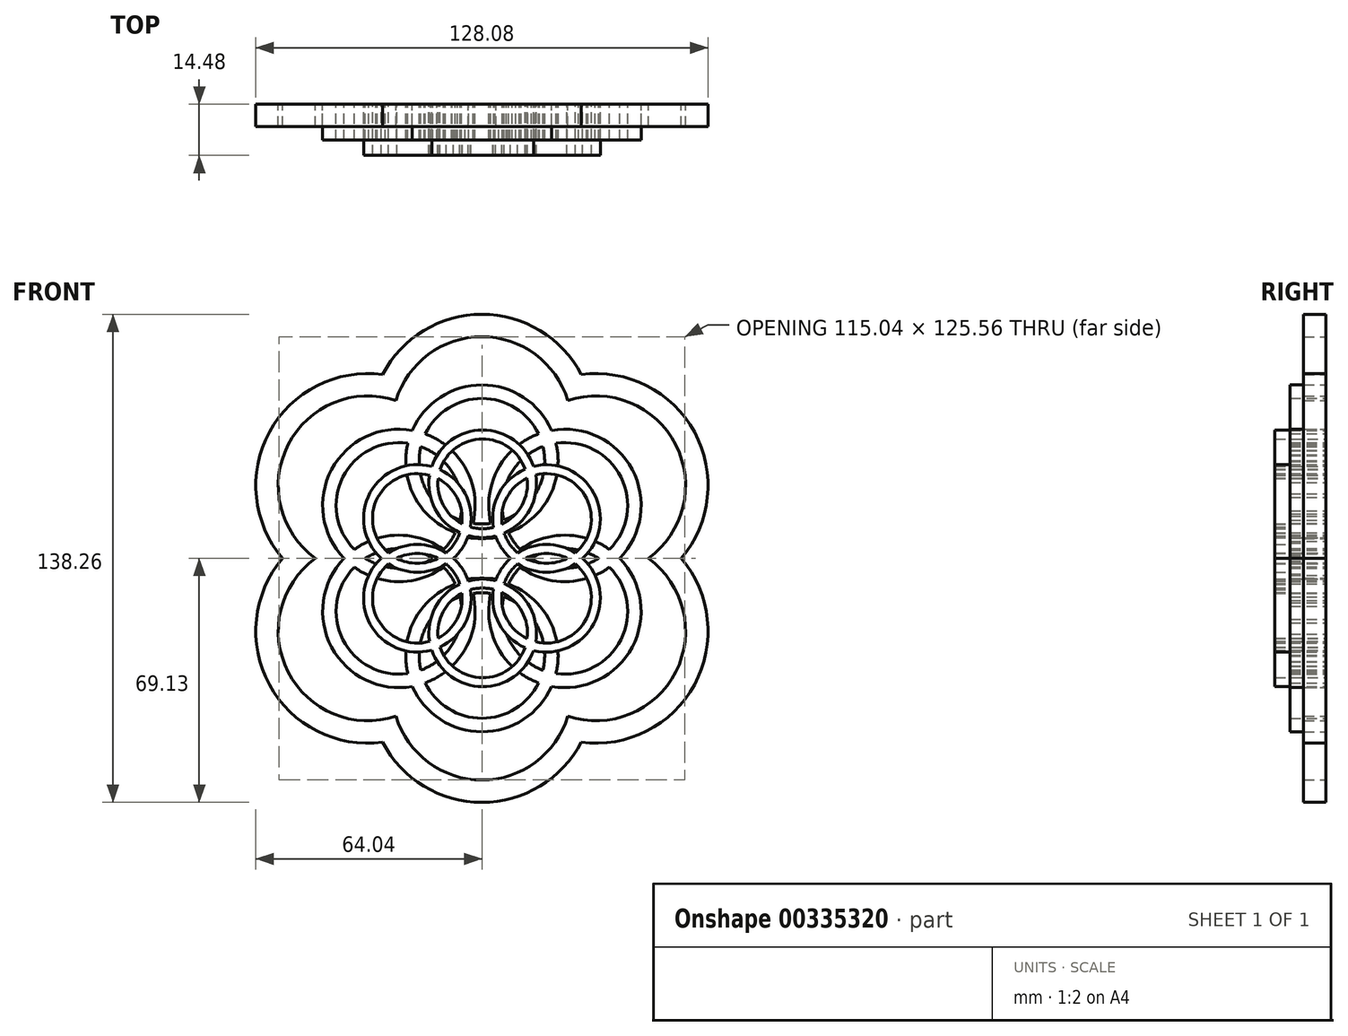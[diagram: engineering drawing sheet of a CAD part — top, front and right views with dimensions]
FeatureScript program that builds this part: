
annotation { "Feature Type Name" : "Feature", "Feature Type Description" : "" }
export const myFeature = defineFeature(function(context is Context, id is Id, definition is map)
    precondition{}
    {
        {
            var Q0;
            Q0=qCreatedBy(makeId("Front.planeOp"),FACE);
            var sketch = newSketch(context, id + "F0", { "sketchPlane" : qUnion([Q0])});
            skArc(sketch, "E0", {"start": v(-1.72, 12.04) * mm, "mid": v(-58.67, 38.27) * mm, "end": v(-12.73, -4.4) * mm});
            skArc(sketch, "E1", {"start": v(-7.98, 13.27) * mm, "mid": v(-52.97, 35.36) * mm, "end": v(-17.44, 0) * mm});
            skArc(sketch, "E2.MirrorC", {"start": v(8.14, 0) * mm, "mid": v(5.98, 2.84) * mm, "end": v(4.15, 5.9) * mm});
            skArc(sketch, "E3.MirrorC", {"start": v(12.73, 4.4) * mm, "mid": v(11.6, 5.88) * mm, "end": v(10.57, 7.44) * mm});
            skArc(sketch, "E4.MirrorC", {"start": v(7.98, -13.27) * mm, "mid": v(52.97, -35.36) * mm, "end": v(17.44, 0) * mm});
            skArc(sketch, "E5.MirrorC", {"start": v(1.72, -12.04) * mm, "mid": v(58.67, -38.27) * mm, "end": v(12.73, 4.4) * mm});
            skArc(sketch, "E6.MirrorC", {"start": v(-8.14, 0) * mm, "mid": v(-5.98, -2.84) * mm, "end": v(-4.15, -5.9) * mm});
            skArc(sketch, "E7.MirrorC", {"start": v(-12.73, -4.4) * mm, "mid": v(-11.6, -5.88) * mm, "end": v(-10.57, -7.44) * mm});
            skArc(sketch, "E8", {"start": v(-4.15, 5.9) * mm, "mid": v(0, 5.63) * mm, "end": v(4.15, 5.9) * mm});
            skArc(sketch, "E9", {"start": v(-1.72, 12.04) * mm, "mid": v(0, 11.98) * mm, "end": v(1.72, 12.04) * mm});
            skArc(sketch, "E10.MirrorC", {"start": v(7.98, -13.27) * mm, "mid": v(0, -62.78) * mm, "end": v(-7.98, -13.27) * mm});
            skArc(sketch, "E11.MirrorC", {"start": v(10.57, -7.44) * mm, "mid": v(0, -69.13) * mm, "end": v(-10.57, -7.44) * mm});
            skArc(sketch, "E12.trimOffspring", {"start": v(7.98, 13.27) * mm, "mid": v(52.97, 35.36) * mm, "end": v(17.44, 0) * mm});
            skArc(sketch, "E13.trimOffspring", {"start": v(1.72, 12.04) * mm, "mid": v(58.67, 38.27) * mm, "end": v(12.73, -4.4) * mm});
            skArc(sketch, "E14.trimOffspring", {"start": v(-1.72, -12.04) * mm, "mid": v(-58.67, -38.27) * mm, "end": v(-12.73, 4.4) * mm});
            skArc(sketch, "E15.trimOffspring", {"start": v(-7.98, -13.27) * mm, "mid": v(-52.97, -35.36) * mm, "end": v(-17.44, 0) * mm});
            skArc(sketch, "E16.trimOffspring", {"start": v(8.14, 0) * mm, "mid": v(5.98, -2.84) * mm, "end": v(4.15, -5.9) * mm});
            skArc(sketch, "E17.trimOffspring", {"start": v(12.73, -4.4) * mm, "mid": v(11.6, -5.88) * mm, "end": v(10.57, -7.44) * mm});
            skArc(sketch, "E18.trimOffspring", {"start": v(-8.14, 0) * mm, "mid": v(-5.98, 2.84) * mm, "end": v(-4.15, 5.9) * mm});
            skArc(sketch, "E19.trimOffspring", {"start": v(-4.15, -5.9) * mm, "mid": v(0, -5.63) * mm, "end": v(4.15, -5.9) * mm});
            skArc(sketch, "E20.trimOffspring", {"start": v(7.98, 13.27) * mm, "mid": v(0, 62.78) * mm, "end": v(-7.98, 13.27) * mm});
            skArc(sketch, "E21.trimOffspring", {"start": v(10.57, 7.44) * mm, "mid": v(0, 69.13) * mm, "end": v(-10.57, 7.44) * mm});
            skArc(sketch, "E22.trimOffspring", {"start": v(-12.73, 4.4) * mm, "mid": v(-11.6, 5.88) * mm, "end": v(-10.57, 7.44) * mm});
            skArc(sketch, "E23.trimOffspring", {"start": v(-1.72, -12.04) * mm, "mid": v(0, -11.98) * mm, "end": v(1.72, -12.04) * mm});
            skSolve(sketch);
        }
        {
            var Q0;
            Q0=qSketchRegion(id+"F0",true);
            var Q1;
            Q1=makeQuery(id+"F0.imprint","IMPRINT",FACE,{"disambiguationData":[TD([[makeQuery(id+"F0.imprint","IMPRINT",EDGE,{"derivedFrom":sQuery(id+"F0.wireOp",EDGE,"E2.MirrorC")}),-1.0]])]});
            var Q2;
            Q2=qSketchRegion(id+"F2",true);
            extrude(context, id + "F1", {"entities" : qUnion([Q0, Q1, Q2]), "depth" : 6.35 * mm});
        }
        {
            var Q0;
            Q0=qCreatedBy(makeId("Front.planeOp"),FACE);
            var sketch = newSketch(context, id + "F2", { "sketchPlane" : qUnion([Q0])});
            skArc(sketch, "E24", {"start": v(-19.74, 36.27) * mm, "mid": v(-42.57, 25.15) * mm, "end": v(-39.03, 0) * mm});
            skArc(sketch, "E25", {"start": v(-20.98, 32.6) * mm, "mid": v(-39.39, 23) * mm, "end": v(-36.14, 2.5) * mm});
            skArc(sketch, "E26.MirrorC", {"start": v(-33.04, 0) * mm, "mid": v(-23.5, 2.77) * mm, "end": v(-13.97, 0) * mm});
            skArc(sketch, "E27.MirrorC", {"start": v(-36.14, 2.5) * mm, "mid": v(-23.5, 6.58) * mm, "end": v(-10.87, 2.5) * mm});
            skArc(sketch, "E28.MirrorC", {"start": v(36.14, 2.5) * mm, "mid": v(23.5, 6.58) * mm, "end": v(10.87, 2.5) * mm});
            skArc(sketch, "E29.MirrorC", {"start": v(33.04, 0) * mm, "mid": v(23.5, 2.77) * mm, "end": v(13.97, 0) * mm});
            skArc(sketch, "E30.MirrorC", {"start": v(20.98, 32.6) * mm, "mid": v(39.39, 23) * mm, "end": v(36.14, 2.5) * mm});
            skArc(sketch, "E31.MirrorC", {"start": v(19.74, 36.27) * mm, "mid": v(42.57, 25.15) * mm, "end": v(39.03, 0) * mm});
            skArc(sketch, "E32", {"start": v(-20.98, 32.6) * mm, "mid": v(-19.06, 17.38) * mm, "end": v(-7.5, 7.28) * mm});
            skArc(sketch, "E33", {"start": v(-17.3, 31.67) * mm, "mid": v(-15.7, 19.17) * mm, "end": v(-6.22, 10.87) * mm});
            skArc(sketch, "E34.MirrorC", {"start": v(7.5, -7.28) * mm, "mid": v(19.06, -17.38) * mm, "end": v(20.98, -32.6) * mm});
            skArc(sketch, "E35.MirrorC", {"start": v(6.22, -10.87) * mm, "mid": v(15.7, -19.17) * mm, "end": v(17.3, -31.67) * mm});
            skArc(sketch, "E36.trimOffspring", {"start": v(-2.52, 9.93) * mm, "mid": v(0, 9.75) * mm, "end": v(2.52, 9.93) * mm});
            skArc(sketch, "E37.trimOffspring", {"start": v(-2.52, 9.93) * mm, "mid": v(-4.45, 25.16) * mm, "end": v(-16.01, 35.26) * mm});
            skArc(sketch, "E38.trimOffspring", {"start": v(-6.22, 10.87) * mm, "mid": v(-7.81, 23.37) * mm, "end": v(-17.3, 31.67) * mm});
            skArc(sketch, "E39.trimOffspring", {"start": v(-3.77, 6.27) * mm, "mid": v(0, 5.94) * mm, "end": v(3.77, 6.27) * mm});
            skArc(sketch, "E40.trimOffspring", {"start": v(-33.04, 0) * mm, "mid": v(-23.5, -2.77) * mm, "end": v(-13.97, 0) * mm});
            skArc(sketch, "E41.trimOffspring", {"start": v(-36.14, -2.5) * mm, "mid": v(-23.5, -6.58) * mm, "end": v(-10.87, -2.5) * mm});
            skArc(sketch, "E42.trimOffspring", {"start": v(-10.87, -2.5) * mm, "mid": v(-8.99, -4.75) * mm, "end": v(-7.5, -7.28) * mm});
            skArc(sketch, "E43.trimOffspring", {"start": v(-7.99, 0) * mm, "mid": v(-5.6, -2.95) * mm, "end": v(-3.77, -6.27) * mm});
            skArc(sketch, "E44.trimOffspring", {"start": v(-7.99, 0) * mm, "mid": v(-5.6, 2.95) * mm, "end": v(-3.77, 6.27) * mm});
            skArc(sketch, "E45.trimOffspring", {"start": v(-10.87, 2.5) * mm, "mid": v(-8.99, 4.75) * mm, "end": v(-7.5, 7.28) * mm});
            skArc(sketch, "E46.trimOffspring", {"start": v(16.01, 35.26) * mm, "mid": v(0, 45.3) * mm, "end": v(-16.01, 35.26) * mm});
            skArc(sketch, "E47.trimOffspring", {"start": v(19.74, 36.27) * mm, "mid": v(0, 49.12) * mm, "end": v(-19.74, 36.27) * mm});
            skArc(sketch, "E48.trimOffspring", {"start": v(33.04, 0) * mm, "mid": v(23.5, -2.77) * mm, "end": v(13.97, 0) * mm});
            skArc(sketch, "E49.trimOffspring", {"start": v(36.14, -2.5) * mm, "mid": v(23.5, -6.58) * mm, "end": v(10.87, -2.5) * mm});
            skArc(sketch, "E50.trimOffspring", {"start": v(10.87, 2.5) * mm, "mid": v(8.99, 4.75) * mm, "end": v(7.5, 7.28) * mm});
            skArc(sketch, "E51.trimOffspring", {"start": v(7.99, 0) * mm, "mid": v(5.6, 2.95) * mm, "end": v(3.77, 6.27) * mm});
            skArc(sketch, "E52.trimOffspring", {"start": v(7.99, 0) * mm, "mid": v(5.6, -2.95) * mm, "end": v(3.77, -6.27) * mm});
            skArc(sketch, "E53.trimOffspring", {"start": v(10.87, -2.5) * mm, "mid": v(8.99, -4.75) * mm, "end": v(7.5, -7.28) * mm});
            skArc(sketch, "E54.trimOffspring", {"start": v(6.22, -10.87) * mm, "mid": v(7.81, -23.37) * mm, "end": v(17.3, -31.67) * mm});
            skArc(sketch, "E55.trimOffspring", {"start": v(2.52, -9.93) * mm, "mid": v(4.45, -25.16) * mm, "end": v(16.01, -35.26) * mm});
            skArc(sketch, "E56.trimOffspring", {"start": v(19.74, -36.27) * mm, "mid": v(0, -49.12) * mm, "end": v(-19.74, -36.27) * mm});
            skArc(sketch, "E57.trimOffspring", {"start": v(20.98, -32.6) * mm, "mid": v(39.39, -23) * mm, "end": v(36.14, -2.5) * mm});
            skArc(sketch, "E58.trimOffspring", {"start": v(16.01, -35.26) * mm, "mid": v(0, -45.3) * mm, "end": v(-16.01, -35.26) * mm});
            skArc(sketch, "E59.trimOffspring", {"start": v(19.74, -36.27) * mm, "mid": v(42.57, -25.15) * mm, "end": v(39.03, 0) * mm});
            skArc(sketch, "E60.trimOffspring", {"start": v(-17.3, -31.67) * mm, "mid": v(-15.7, -19.17) * mm, "end": v(-6.22, -10.87) * mm});
            skArc(sketch, "E61.trimOffspring", {"start": v(-20.98, -32.6) * mm, "mid": v(-39.39, -23) * mm, "end": v(-36.14, -2.5) * mm});
            skArc(sketch, "E62.trimOffspring", {"start": v(-20.98, -32.6) * mm, "mid": v(-19.06, -17.38) * mm, "end": v(-7.5, -7.28) * mm});
            skArc(sketch, "E63.trimOffspring", {"start": v(-19.74, -36.27) * mm, "mid": v(-42.57, -25.15) * mm, "end": v(-39.03, 0) * mm});
            skArc(sketch, "E64.trimOffspring", {"start": v(-2.52, -9.93) * mm, "mid": v(0, -9.75) * mm, "end": v(2.52, -9.93) * mm});
            skArc(sketch, "E65.trimOffspring", {"start": v(-3.77, -6.27) * mm, "mid": v(0, -5.94) * mm, "end": v(3.77, -6.27) * mm});
            skArc(sketch, "E66.trimOffspring", {"start": v(-6.22, -10.87) * mm, "mid": v(-7.81, -23.37) * mm, "end": v(-17.3, -31.67) * mm});
            skArc(sketch, "E67.trimOffspring", {"start": v(-2.52, -9.93) * mm, "mid": v(-4.45, -25.16) * mm, "end": v(-16.01, -35.26) * mm});
            skArc(sketch, "E68.trimOffspring", {"start": v(2.52, 9.93) * mm, "mid": v(4.45, 25.16) * mm, "end": v(16.01, 35.26) * mm});
            skArc(sketch, "E69.trimOffspring", {"start": v(6.22, 10.87) * mm, "mid": v(15.7, 19.17) * mm, "end": v(17.3, 31.67) * mm});
            skArc(sketch, "E70.trimOffspring", {"start": v(7.5, 7.28) * mm, "mid": v(19.06, 17.38) * mm, "end": v(20.98, 32.6) * mm});
            skArc(sketch, "E71.trimOffspring", {"start": v(6.22, 10.87) * mm, "mid": v(7.81, 23.37) * mm, "end": v(17.3, 31.67) * mm});
            skSolve(sketch);
        }
        {
            var Q0;
            Q0=makeQuery(id+"F2.imprint","IMPRINT",FACE,{"disambiguationData":[TD([[makeQuery(id+"F2.imprint","IMPRINT",EDGE,{"derivedFrom":sQuery(id+"F2.wireOp",EDGE,"E24")}),1.0]])]});
            extrude(context, id + "F3", {"entities" : qUnion([Q0]), "operationType" : NewBodyOperationType.ADD, "depth" : 5.08 * mm});
        }
        {
            var Q0;
            Q0=qCreatedBy(makeId("Front.planeOp"),FACE);
            var sketch = newSketch(context, id + "F4", { "sketchPlane" : qUnion([Q0])});
            skArc(sketch, "E72", {"start": v(-14.23, 25.99) * mm, "mid": v(-31.65, 18.64) * mm, "end": v(-28.52, 0) * mm});
            skArc(sketch, "E73", {"start": v(-14.84, 23.52) * mm, "mid": v(-29.52, 17.24) * mm, "end": v(-26.45, 1.57) * mm});
            skArc(sketch, "E74", {"start": v(-14.84, 23.52) * mm, "mid": v(-13.26, 13.97) * mm, "end": v(-6.24, 7.3) * mm});
            skArc(sketch, "E75", {"start": v(-12.41, 22.56) * mm, "mid": v(-11.01, 15.16) * mm, "end": v(-5.67, 9.85) * mm});
            skArc(sketch, "E76.MirrorC", {"start": v(-12.41, -22.56) * mm, "mid": v(-11.01, -15.16) * mm, "end": v(-5.67, -9.85) * mm});
            skArc(sketch, "E77.MirrorC", {"start": v(-14.84, -23.52) * mm, "mid": v(-13.26, -13.97) * mm, "end": v(-6.24, -7.3) * mm});
            skArc(sketch, "E78.MirrorC", {"start": v(24.09, 0) * mm, "mid": v(18.3, -1.4) * mm, "end": v(12.5, 0) * mm});
            skArc(sketch, "E79.MirrorC", {"start": v(26.45, -1.57) * mm, "mid": v(18.3, -3.94) * mm, "end": v(10.13, -1.57) * mm});
            skArc(sketch, "E80.MirrorC", {"start": v(5.7, -9.66) * mm, "mid": v(7.13, -17.36) * mm, "end": v(12.8, -22.75) * mm});
            skArc(sketch, "E81.MirrorC", {"start": v(3.26, -8.78) * mm, "mid": v(4.9, -18.57) * mm, "end": v(12.2, -25.27) * mm});
            skArc(sketch, "E82.MirrorC", {"start": v(-24.09, 0) * mm, "mid": v(-18.3, 1.4) * mm, "end": v(-12.5, 0) * mm});
            skArc(sketch, "E83.MirrorC", {"start": v(-26.45, 1.57) * mm, "mid": v(-18.3, 3.94) * mm, "end": v(-10.13, 1.57) * mm});
            skArc(sketch, "E84.trimOffspring", {"start": v(-3.85, 6.42) * mm, "mid": v(0.01, 5.87) * mm, "end": v(3.89, 6.32) * mm});
            skArc(sketch, "E85.trimOffspring", {"start": v(-3.24, 8.89) * mm, "mid": v(0, 8.41) * mm, "end": v(3.26, 8.78) * mm});
            skArc(sketch, "E86.trimOffspring", {"start": v(-5.67, 9.85) * mm, "mid": v(-7.07, 17.25) * mm, "end": v(-12.41, 22.56) * mm});
            skArc(sketch, "E87.trimOffspring", {"start": v(-3.24, 8.89) * mm, "mid": v(-4.83, 18.44) * mm, "end": v(-11.85, 25.11) * mm});
            skArc(sketch, "E88.trimOffspring", {"start": v(-26.45, -1.57) * mm, "mid": v(-18.3, -3.94) * mm, "end": v(-10.13, -1.57) * mm});
            skArc(sketch, "E89.trimOffspring", {"start": v(-24.09, 0) * mm, "mid": v(-18.3, -1.4) * mm, "end": v(-12.5, 0) * mm});
            skArc(sketch, "E90.trimOffspring", {"start": v(-14.84, -23.52) * mm, "mid": v(-29.52, -17.24) * mm, "end": v(-26.45, -1.57) * mm});
            skArc(sketch, "E91.trimOffspring", {"start": v(-14.23, -25.99) * mm, "mid": v(-31.65, -18.64) * mm, "end": v(-28.52, 0) * mm});
            skArc(sketch, "E92.trimOffspring", {"start": v(-3.85, -6.42) * mm, "mid": v(0.01, -5.87) * mm, "end": v(3.89, -6.32) * mm});
            skArc(sketch, "E93.trimOffspring", {"start": v(-5.67, -9.85) * mm, "mid": v(-7.07, -17.25) * mm, "end": v(-12.41, -22.56) * mm});
            skArc(sketch, "E94.trimOffspring", {"start": v(-3.24, -8.89) * mm, "mid": v(0, -8.41) * mm, "end": v(3.26, -8.78) * mm});
            skArc(sketch, "E95.trimOffspring", {"start": v(-3.24, -8.89) * mm, "mid": v(-4.83, -18.44) * mm, "end": v(-11.85, -25.11) * mm});
            skArc(sketch, "E96.trimOffspring", {"start": v(5.7, -9.66) * mm, "mid": v(11.37, -15.05) * mm, "end": v(12.8, -22.75) * mm});
            skArc(sketch, "E97.trimOffspring", {"start": v(6.3, -7.14) * mm, "mid": v(13.6, -13.84) * mm, "end": v(15.24, -23.63) * mm});
            skArc(sketch, "E98.trimOffspring", {"start": v(15.24, -23.63) * mm, "mid": v(29.61, -17.06) * mm, "end": v(26.45, -1.57) * mm});
            skArc(sketch, "E99.trimOffspring", {"start": v(12.2, -25.27) * mm, "mid": v(0.12, -33.8) * mm, "end": v(-11.85, -25.11) * mm});
            skArc(sketch, "E100.trimOffspring", {"start": v(14.6, -26.09) * mm, "mid": v(31.74, -18.47) * mm, "end": v(28.52, 0) * mm});
            skArc(sketch, "E101.trimOffspring", {"start": v(14.6, -26.09) * mm, "mid": v(0.15, -36.35) * mm, "end": v(-14.23, -25.99) * mm});
            skArc(sketch, "E102.trimOffspring", {"start": v(26.45, 1.57) * mm, "mid": v(18.3, 3.94) * mm, "end": v(10.13, 1.57) * mm});
            skArc(sketch, "E103.trimOffspring", {"start": v(24.09, 0) * mm, "mid": v(18.3, 1.4) * mm, "end": v(12.5, 0) * mm});
            skArc(sketch, "E104.trimOffspring", {"start": v(8.07, 0) * mm, "mid": v(5.58, -2.9) * mm, "end": v(3.89, -6.32) * mm});
            skArc(sketch, "E105.trimOffspring", {"start": v(8.07, 0) * mm, "mid": v(5.58, 2.9) * mm, "end": v(3.89, 6.32) * mm});
            skArc(sketch, "E106.trimOffspring", {"start": v(10.13, 1.57) * mm, "mid": v(7.83, 4.1) * mm, "end": v(6.3, 7.14) * mm});
            skArc(sketch, "E107.trimOffspring", {"start": v(10.13, -1.57) * mm, "mid": v(7.83, -4.1) * mm, "end": v(6.3, -7.14) * mm});
            skArc(sketch, "E108.trimOffspring", {"start": v(6.3, 7.14) * mm, "mid": v(13.6, 13.84) * mm, "end": v(15.24, 23.63) * mm});
            skArc(sketch, "E109.trimOffspring", {"start": v(5.7, 9.66) * mm, "mid": v(11.37, 15.05) * mm, "end": v(12.8, 22.75) * mm});
            skArc(sketch, "E110.trimOffspring", {"start": v(5.7, 9.66) * mm, "mid": v(7.13, 17.36) * mm, "end": v(12.8, 22.75) * mm});
            skArc(sketch, "E111.trimOffspring", {"start": v(3.26, 8.78) * mm, "mid": v(4.9, 18.57) * mm, "end": v(12.2, 25.27) * mm});
            skArc(sketch, "E112.trimOffspring", {"start": v(12.2, 25.27) * mm, "mid": v(0.12, 33.8) * mm, "end": v(-11.85, 25.11) * mm});
            skArc(sketch, "E113.trimOffspring", {"start": v(14.6, 26.09) * mm, "mid": v(31.74, 18.47) * mm, "end": v(28.52, 0) * mm});
            skArc(sketch, "E114.trimOffspring", {"start": v(14.6, 26.09) * mm, "mid": v(0.15, 36.35) * mm, "end": v(-14.23, 25.99) * mm});
            skArc(sketch, "E115.trimOffspring", {"start": v(15.24, 23.63) * mm, "mid": v(29.61, 17.06) * mm, "end": v(26.45, 1.57) * mm});
            skArc(sketch, "E116.trimOffspring", {"start": v(-8.07, 0) * mm, "mid": v(-5.55, -2.94) * mm, "end": v(-3.85, -6.42) * mm});
            skArc(sketch, "E117.trimOffspring", {"start": v(-10.13, 1.57) * mm, "mid": v(-7.79, 4.16) * mm, "end": v(-6.24, 7.3) * mm});
            skArc(sketch, "E118.trimOffspring", {"start": v(-10.13, -1.57) * mm, "mid": v(-7.79, -4.16) * mm, "end": v(-6.24, -7.3) * mm});
            skArc(sketch, "E119.trimOffspring", {"start": v(-8.07, 0) * mm, "mid": v(-5.55, 2.94) * mm, "end": v(-3.85, 6.42) * mm});
            skSolve(sketch);
        }
        {
            var Q0;
            Q0=qSketchRegion(id+"F4",true);
            extrude(context, id + "F5", {"entities" : qUnion([Q0]), "depth" : 3.8 * mm});
        }
        {
            var Q0;
            Q0=qSketchRegion(id+"F2",true);
            extrude(context, id + "F6", {"entities" : qUnion([Q0]), "operationType" : NewBodyOperationType.ADD, "depth" : 10.16 * mm});
        }
        {
            var Q0;
            Q0=qSketchRegion(id+"F4",true);
            extrude(context, id + "F7", {"entities" : qUnion([Q0]), "operationType" : NewBodyOperationType.ADD, "depth" : 14.48 * mm});
        }
    });
